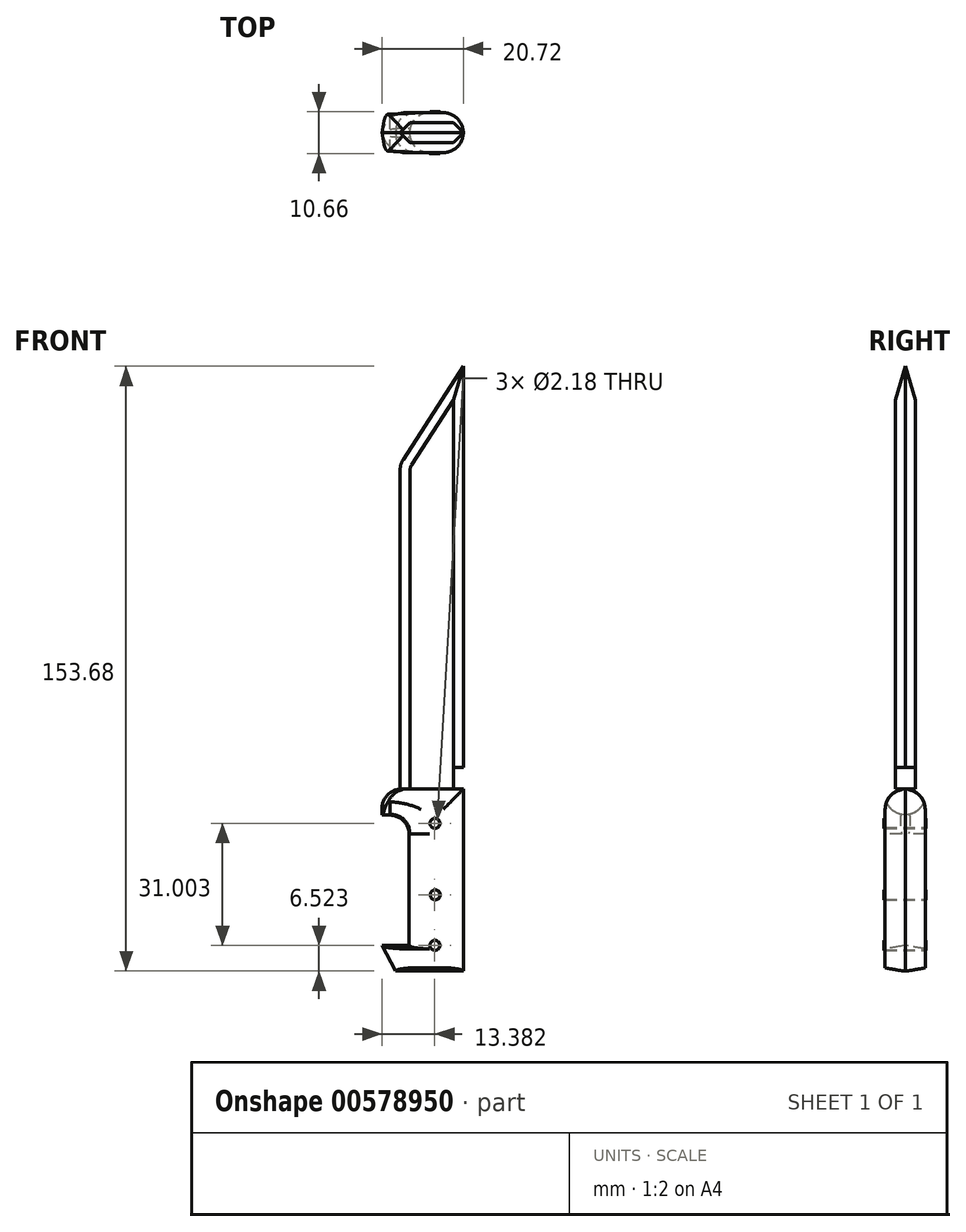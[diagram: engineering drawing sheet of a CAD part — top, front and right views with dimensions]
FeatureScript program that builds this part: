
annotation { "Feature Type Name" : "Feature", "Feature Type Description" : "" }
export const myFeature = defineFeature(function(context is Context, id is Id, definition is map)
    precondition{}
    {
        {
            var Q0;
            Q0=qCreatedBy(makeId("Front.planeOp"),FACE);
            var sketch = newSketch(context, id + "F0", { "sketchPlane" : qUnion([Q0])});
            skLineSegment(sketch, "E0", {"start": v(-11.51, 11.22) * mm, "end": v(-20.72, 11.22) * mm});
            skLineSegment(sketch, "E1", {"start": v(-20.72, 11.22) * mm, "end": v(-20.72, 4.6) * mm});
            skLineSegment(sketch, "E2", {"start": v(-20.72, 4.6) * mm, "end": v(-13.81, 4.6) * mm});
            skLineSegment(sketch, "E3", {"start": v(-13.81, 4.6) * mm, "end": v(-13.81, -28.5) * mm});
            skLineSegment(sketch, "E4", {"start": v(-13.81, -28.5) * mm, "end": v(-20.72, -28.5) * mm});
            skLineSegment(sketch, "E5", {"start": v(-20.72, -28.5) * mm, "end": v(-17.27, -35.11) * mm});
            skLineSegment(sketch, "E6", {"start": v(-17.27, -35.11) * mm, "end": v(0, -35.11) * mm});
            skLineSegment(sketch, "E7", {"start": v(0, -8.35) * mm, "end": v(0, 4.6) * mm});
            skLineSegment(sketch, "E8", {"start": v(0, 4.6) * mm, "end": v(0, 11.22) * mm});
            skLineSegment(sketch, "E9", {"start": v(0, 11.22) * mm, "end": v(-11.51, 11.22) * mm});
            skLineSegment(sketch, "E10", {"start": v(0, -8.35) * mm, "end": v(0, -35.11) * mm});
            skLineSegment(sketch, "E11", {"start": v(-16.12, 11.22) * mm, "end": v(-16.12, 59.58) * mm});
            skLineSegment(sketch, "E12", {"start": v(-2.6, 11.22) * mm, "end": v(-2.6, 16.7) * mm});
            skLineSegment(sketch, "E13", {"start": v(-2.6, 16.7) * mm, "end": v(0, 16.7) * mm});
            skLineSegment(sketch, "E14", {"start": v(0, 16.7) * mm, "end": v(0, 118.65) * mm});
            skLineSegment(sketch, "E15", {"start": v(0, 118.65) * mm, "end": v(-15.3, 94.98) * mm});
            skLineSegment(sketch, "E16", {"start": v(-16.12, 92.23) * mm, "end": v(-16.12, 59.58) * mm});
            skPoint(sketch, "E17.visualSharp", {"position": v(-16.12, 93.73) * mm});
            skArc(sketch, "E17.filletArc", {"start": v(-15.3, 94.98) * mm, "mid": v(-15.9, 93.66) * mm, "end": v(-16.12, 92.23) * mm});
            skSolve(sketch);
        }
        {
            var Q0;
            {var subQ5=sQuery(id+"F0.wireOp",EDGE,"E1");Q0=makeQuery(id+"F0.imprint","IMPRINT",FACE,{"disambiguationData":[TD([[makeQuery(id+"F0.imprint","IMPRINT",EDGE,{"derivedFrom":subQ5}),1.0]])]});}
            extrude(context, id + "F1", {"entities" : qUnion([Q0]), "oppositeDirection" : true, "depth" : 5.08 * mm, "offsetDistance" : 25.4 * mm, "hasDraft" : true, "draftAngle" : 10 * degree, "draftPullDirection" : true, "hasSecondDirection" : true, "secondDirectionOppositeDirection" : false, "secondDirectionDepth" : 5.08 * mm, "hasSecondDirectionDraft" : true, "secondDirectionDraftAngle" : 10 * degree, "secondDirectionDraftPullDirection" : true});
        }
        {
            var Q0;
            Q0=makeQuery(id+"F1.opExtrude","CAP_EDGE",EDGE,{"disambiguationData":[OSD([sQuery(id+"F0.wireOp",EDGE,"E7"),sQuery(id+"F0.wireOp",EDGE,"E8"),sQuery(id+"F0.wireOp",EDGE,"E10")])],"isStart":false});
            var Q1;
            Q1=makeQuery(id+"F1.opExtrude","CAP_EDGE",EDGE,{"disambiguationData":[OSD([sQuery(id+"F0.wireOp",EDGE,"E0"),sQuery(id+"F0.wireOp",EDGE,"E9")])],"isStart":false});
            var Q2;
            Q2=makeQuery(id+"F1.opExtrude","CAP_EDGE",EDGE,{"disambiguationData":[OSD([sQuery(id+"F0.wireOp",EDGE,"E2")])],"isStart":false});
            var Q3;
            Q3=makeQuery(id+"F1.opExtrude","CAP_EDGE",EDGE,{"disambiguationData":[OSD([sQuery(id+"F0.wireOp",EDGE,"E3")])],"isStart":false});
            var Q4;
            Q4=makeQuery(id+"F1.opExtrude","CAP_EDGE",EDGE,{"disambiguationData":[OSD([sQuery(id+"F0.wireOp",EDGE,"E0"),sQuery(id+"F0.wireOp",EDGE,"E9")])],"isStart":true});
            var Q5;
            Q5=makeQuery(id+"F1.opExtrude","CAP_EDGE",EDGE,{"disambiguationData":[OSD([sQuery(id+"F0.wireOp",EDGE,"E3")])],"isStart":true});
            var Q6;
            Q6=makeQuery(id+"F1.opExtrude","CAP_EDGE",EDGE,{"disambiguationData":[OSD([sQuery(id+"F0.wireOp",EDGE,"E5")])],"isStart":false});
            var Q7;
            Q7=makeQuery(id+"F1.opExtrude","CAP_EDGE",EDGE,{"disambiguationData":[OSD([sQuery(id+"F0.wireOp",EDGE,"E5")])],"isStart":true});
            var Q8;
            {var subQ0=makeQuery(id+"F1.opExtrude","SWEPT_FACE",FACE,{"disambiguationData":[OSD([sQuery(id+"F0.wireOp",EDGE,"E6")])]});Q8=makeQuery(id+"F1.*.booleanUnion.opBoolean","MERGE",EDGE,{"derivedFrom":[makeQuery(id+"F1.*.split.splitOp","SPLIT_SURFACE_INTERSECT",EDGE,{"derivedFrom":[subQ0]}),makeQuery(id+"F1.*.split.splitOp","SPLIT_SURFACE_INTERSECT",EDGE,{"derivedFrom":[subQ0],"isFromBackBody":true})]});}
            var Q9;
            Q9=makeQuery(id+"F1.opExtrude","CAP_EDGE",EDGE,{"disambiguationData":[OSD([sQuery(id+"F0.wireOp",EDGE,"E7"),sQuery(id+"F0.wireOp",EDGE,"E8"),sQuery(id+"F0.wireOp",EDGE,"E10")])],"isStart":true});
            var Q10;
            Q10=makeQuery(id+"F1.opExtrude","CAP_EDGE",EDGE,{"disambiguationData":[OSD([sQuery(id+"F0.wireOp",EDGE,"E2")])],"isStart":true});
            var Q11;
            Q11=makeQuery(id+"F1.*.split.splitOp","SPLIT",EDGE,{"derivedFrom":makeQuery(id+"F1.opExtrude","SWEPT_EDGE",EDGE,{"disambiguationData":[OSD([sQuery(id+"F0.wireOp",EDGE,"E2"),sQuery(id+"F0.wireOp",EDGE,"E3")])]})});
            var Q12;
            Q12=makeQuery(id+"F1.*.split.splitOp","SPLIT",EDGE,{"derivedFrom":makeQuery(id+"F1.opExtrude","SWEPT_EDGE",EDGE,{"disambiguationData":[OSD([sQuery(id+"F0.wireOp",EDGE,"E2"),sQuery(id+"F0.wireOp",EDGE,"E3")])]}),"isFromBackBody":true});
            var Q13;
            Q13=makeQuery(id+"F1.*.split.splitOp","SPLIT",EDGE,{"derivedFrom":makeQuery(id+"F1.opExtrude","SWEPT_EDGE",EDGE,{"disambiguationData":[OSD([sQuery(id+"F0.wireOp",EDGE,"E0"),sQuery(id+"F0.wireOp",EDGE,"E1")])]})});
            var Q14;
            Q14=makeQuery(id+"F1.*.split.splitOp","SPLIT",EDGE,{"derivedFrom":makeQuery(id+"F1.opExtrude","SWEPT_EDGE",EDGE,{"disambiguationData":[OSD([sQuery(id+"F0.wireOp",EDGE,"E0"),sQuery(id+"F0.wireOp",EDGE,"E1")])]}),"isFromBackBody":true});
            fillet(context, id + "F2", {"entities" : qUnion([Q0, Q1, Q2, Q3, Q4, Q5, Q6, Q7, Q8, Q9, Q10, Q11, Q12, Q13, Q14]), "radius" : 5.08 * mm, "tangentPropagation" : true, "allowEdgeOverflow" : false});
        }
        {
            var Q0;
            Q0=qCreatedBy(makeId("Front.planeOp"),FACE);
            var sketch = newSketch(context, id + "F3", { "sketchPlane" : qUnion([Q0])});
            skCircle(sketch, "E18", {"center": v(-7.34, 2.5) * mm, "radius": 1.09 * mm});
            skCircle(sketch, "E19", {"center": v(-7.34, -15.7) * mm, "radius": 1.09 * mm});
            skCircle(sketch, "E20", {"center": v(-7.34, -28.5) * mm, "radius": 1.09 * mm});
            skSolve(sketch);
        }
        {
            var Q0;
            Q0 = qSketchRegion(id + "F3", true);
            extrude(context, id + "F4", {"entities" : qUnion([Q0]), "operationType" : NewBodyOperationType.REMOVE, "depth" : 25.4 * mm, "offsetDistance" : 25.4 * mm, "hasSecondDirection" : true, "secondDirectionOppositeDirection" : true, "secondDirectionDepth" : 25.4 * mm});
        }
        {
            var Q0;
            {var subQ1=sQuery(id+"F0.wireOp",EDGE,"E11");Q0=makeQuery(id+"F0.imprint","IMPRINT",FACE,{"disambiguationData":[TD([[makeQuery(id+"F0.imprint","IMPRINT",EDGE,{"derivedFrom":subQ1}),-1.0]])]});}
            extrude(context, id + "F5", {"entities" : qUnion([Q0]), "depth" : 2.54 * mm, "offsetDistance" : 25.4 * mm, "hasSecondDirection" : true, "secondDirectionOppositeDirection" : true, "secondDirectionDepth" : 2.54 * mm});
        }
        {
            var Q0;
            Q0=makeQuery(id+"F5.opExtrude","CAP_EDGE",EDGE,{"disambiguationData":[OSD([sQuery(id+"F0.wireOp",EDGE,"E14")])],"isStart":true});
            var Q1;
            Q1=makeQuery(id+"F5.opExtrude","CAP_EDGE",EDGE,{"disambiguationData":[OSD([sQuery(id+"F0.wireOp",EDGE,"E15")])],"isStart":true});
            var Q2;
            Q2=makeQuery(id+"F5.opExtrude","CAP_EDGE",EDGE,{"disambiguationData":[OSD([sQuery(id+"F0.wireOp",EDGE,"E15")])],"isStart":false});
            var Q3;
            Q3=makeQuery(id+"F5.opExtrude","CAP_EDGE",EDGE,{"disambiguationData":[OSD([sQuery(id+"F0.wireOp",EDGE,"E14")])],"isStart":false});
            chamfer(context, id + "F6", {"entities" : qUnion([Q0, Q1, Q2, Q3]), "width" : 2.54 * mm, "tangentPropagation" : true});
        }
        {
            var Q0;
            Q0=qCreatedBy(makeId("Front.planeOp"),FACE);
            var sketch = newSketch(context, id + "F7", { "sketchPlane" : qUnion([Q0])});
            skCircle(sketch, "E21", {"center": v(-7.26, 2.5) * mm, "radius": 1.27 * mm});
            skCircle(sketch, "E22", {"center": v(-7.2, -15.67) * mm, "radius": 1.27 * mm});
            skCircle(sketch, "E23", {"center": v(-7.27, -28.5) * mm, "radius": 1.27 * mm});
            skSolve(sketch);
        }
        {
            var Q0;
            Q0 = qSketchRegion(id + "F7", true);
            extrude(context, id + "F8", {"entities" : qUnion([Q0]), "depth" : 5.33 * mm, "offsetDistance" : 25.4 * mm, "hasSecondDirection" : true, "secondDirectionOppositeDirection" : true, "secondDirectionDepth" : 5.33 * mm});
        }
    });
